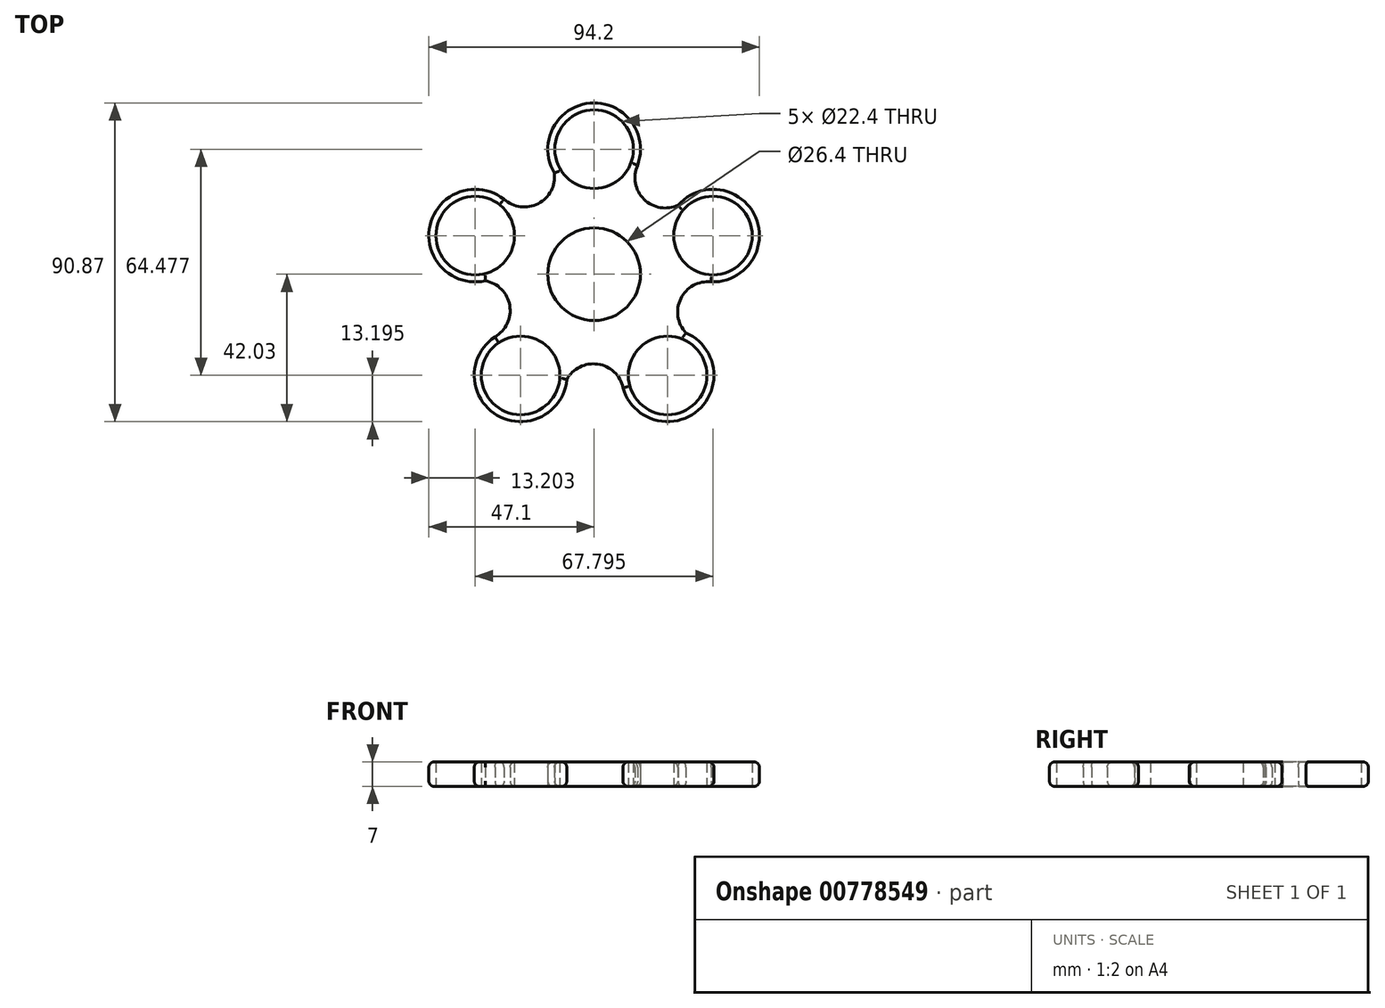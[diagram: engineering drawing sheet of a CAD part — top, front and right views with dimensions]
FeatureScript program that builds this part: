
annotation { "Feature Type Name" : "Feature", "Feature Type Description" : "" }
export const myFeature = defineFeature(function(context is Context, id is Id, definition is map)
    precondition{}
    {
        {
            var Q0;
            Q0=qCreatedBy(makeId("Top.planeOp"),FACE);
            var sketch = newSketch(context, id + "F0", { "sketchPlane" : qUnion([Q0])});
            skCircle(sketch, "E0", {"center": v(0, 0) * mm, "radius": 11.2 * mm});
            skCircle(sketch, "E1", {"center": v(0, 0) * mm, "radius": 13.2 * mm});
            skCircle(sketch, "E2", {"center": v(0, 35.64) * mm, "radius": 11.2 * mm});
            skCircle(sketch, "E3", {"center": v(0, 35.64) * mm, "radius": 13.2 * mm});
            skCircle(sketch, "E4.1.0", {"center": v(-33.9, 11.01) * mm, "radius": 11.2 * mm});
            skCircle(sketch, "E4.1.1", {"center": v(-33.9, 11.01) * mm, "radius": 13.2 * mm});
            skCircle(sketch, "E4.2.0", {"center": v(-20.95, -28.83) * mm, "radius": 11.2 * mm});
            skCircle(sketch, "E4.2.1", {"center": v(-20.95, -28.83) * mm, "radius": 13.2 * mm});
            skCircle(sketch, "E4.3.0", {"center": v(20.95, -28.83) * mm, "radius": 11.2 * mm});
            skCircle(sketch, "E4.3.1", {"center": v(20.95, -28.83) * mm, "radius": 13.2 * mm});
            skCircle(sketch, "E4.4.0", {"center": v(33.9, 11.01) * mm, "radius": 11.2 * mm});
            skCircle(sketch, "E4.4.1", {"center": v(33.9, 11.01) * mm, "radius": 13.2 * mm});
            skArc(sketch, "E5", {"start": v(12.37, 31.05) * mm, "mid": v(14.23, 21.35) * mm, "end": v(23.97, 19.71) * mm});
            skArc(sketch, "E6.1.0", {"start": v(-25.7, 21.36) * mm, "mid": v(-15.9, 20.13) * mm, "end": v(-11.34, 28.89) * mm});
            skArc(sketch, "E6.2.0", {"start": v(-28.26, -17.84) * mm, "mid": v(-24.06, -8.9) * mm, "end": v(-30.98, -1.86) * mm});
            skArc(sketch, "E6.3.0", {"start": v(8.24, -32.4) * mm, "mid": v(1.04, -25.64) * mm, "end": v(-7.8, -30.04) * mm});
            skArc(sketch, "E6.4.0", {"start": v(33.35, -2.17) * mm, "mid": v(24.7, -6.94) * mm, "end": v(26.15, -16.7) * mm});
            skSolve(sketch);
        }
        {
            var Q0;
            Q0=makeQuery(id+"F0.imprint","IMPRINT",FACE,{"disambiguationData":[TD([[makeQuery(id+"F0.imprint","IMPRINT",EDGE,{"derivedFrom":sQuery(id+"F0.wireOp",EDGE,"E1")}),-1.0]])]});
            var Q1;
            Q1=makeQuery(id+"F0.imprint","IMPRINT",FACE,{"disambiguationData":[TD([[makeQuery(id+"F0.imprint","IMPRINT",EDGE,{"derivedFrom":sQuery(id+"F0.wireOp",EDGE,"E4.2.0")}),-1.0]])]});
            var Q2;
            Q2=makeQuery(id+"F0.imprint","IMPRINT",FACE,{"disambiguationData":[TD([[makeQuery(id+"F0.imprint","IMPRINT",EDGE,{"derivedFrom":sQuery(id+"F0.wireOp",EDGE,"E4.3.0")}),-1.0]])]});
            var Q3;
            Q3=makeQuery(id+"F0.imprint","IMPRINT",FACE,{"disambiguationData":[TD([[makeQuery(id+"F0.imprint","IMPRINT",EDGE,{"derivedFrom":sQuery(id+"F0.wireOp",EDGE,"E4.4.0")}),-1.0]])]});
            var Q4;
            Q4=makeQuery(id+"F0.imprint","IMPRINT",FACE,{"disambiguationData":[TD([[makeQuery(id+"F0.imprint","IMPRINT",EDGE,{"derivedFrom":sQuery(id+"F0.wireOp",EDGE,"E2")}),-1.0]])]});
            var Q5;
            Q5=makeQuery(id+"F0.imprint","IMPRINT",FACE,{"disambiguationData":[TD([[makeQuery(id+"F0.imprint","IMPRINT",EDGE,{"derivedFrom":sQuery(id+"F0.wireOp",EDGE,"E4.1.0")}),-1.0]])]});
            extrude(context, id + "F1", {"entities" : qUnion([Q0, Q1, Q2, Q3, Q4, Q5]), "depth" : 7 * mm, "offsetDistance" : 25 * mm});
        }
        {
            var Q0;
            Q0=makeQuery(id+"F1.opExtrude","CAP_EDGE",EDGE,{"disambiguationData":[OSD([sQuery(id+"F0.wireOp",EDGE,"E5")])],"isStart":true});
            var Q1;
            Q1=makeQuery(id+"F1.opExtrude","CAP_EDGE",EDGE,{"disambiguationData":[OSD([sQuery(id+"F0.wireOp",EDGE,"E4.4.1")])],"isStart":true});
            var Q2;
            Q2=makeQuery(id+"F1.opExtrude","CAP_EDGE",EDGE,{"disambiguationData":[OSD([sQuery(id+"F0.wireOp",EDGE,"E6.4.0")])],"isStart":true});
            var Q3;
            Q3=makeQuery(id+"F1.opExtrude","CAP_EDGE",EDGE,{"disambiguationData":[OSD([sQuery(id+"F0.wireOp",EDGE,"E4.3.1")])],"isStart":true});
            var Q4;
            Q4=makeQuery(id+"F1.opExtrude","CAP_EDGE",EDGE,{"disambiguationData":[OSD([sQuery(id+"F0.wireOp",EDGE,"E6.3.0")])],"isStart":true});
            var Q5;
            Q5=makeQuery(id+"F1.opExtrude","CAP_EDGE",EDGE,{"disambiguationData":[OSD([sQuery(id+"F0.wireOp",EDGE,"E4.2.1")])],"isStart":true});
            var Q6;
            Q6=makeQuery(id+"F1.opExtrude","CAP_EDGE",EDGE,{"disambiguationData":[OSD([sQuery(id+"F0.wireOp",EDGE,"E6.2.0")])],"isStart":true});
            var Q7;
            Q7=makeQuery(id+"F1.opExtrude","CAP_EDGE",EDGE,{"disambiguationData":[OSD([sQuery(id+"F0.wireOp",EDGE,"E4.1.1")])],"isStart":true});
            var Q8;
            Q8=makeQuery(id+"F1.opExtrude","CAP_EDGE",EDGE,{"disambiguationData":[OSD([sQuery(id+"F0.wireOp",EDGE,"E3")])],"isStart":true});
            var Q9;
            Q9=makeQuery(id+"F1.opExtrude","CAP_EDGE",EDGE,{"disambiguationData":[OSD([sQuery(id+"F0.wireOp",EDGE,"E6.1.0")])],"isStart":true});
            var Q10;
            Q10=makeQuery(id+"F1.opExtrude","CAP_EDGE",EDGE,{"disambiguationData":[OSD([sQuery(id+"F0.wireOp",EDGE,"E5")])],"isStart":false});
            var Q11;
            Q11=makeQuery(id+"F1.opExtrude","CAP_EDGE",EDGE,{"disambiguationData":[OSD([sQuery(id+"F0.wireOp",EDGE,"E4.1.1")])],"isStart":false});
            var Q12;
            Q12=makeQuery(id+"F1.opExtrude","CAP_EDGE",EDGE,{"disambiguationData":[OSD([sQuery(id+"F0.wireOp",EDGE,"E6.1.0")])],"isStart":false});
            var Q13;
            Q13=makeQuery(id+"F1.opExtrude","CAP_EDGE",EDGE,{"disambiguationData":[OSD([sQuery(id+"F0.wireOp",EDGE,"E3")])],"isStart":false});
            var Q14;
            Q14=makeQuery(id+"F1.opExtrude","CAP_EDGE",EDGE,{"disambiguationData":[OSD([sQuery(id+"F0.wireOp",EDGE,"E4.4.1")])],"isStart":false});
            var Q15;
            Q15=makeQuery(id+"F1.opExtrude","CAP_EDGE",EDGE,{"disambiguationData":[OSD([sQuery(id+"F0.wireOp",EDGE,"E6.4.0")])],"isStart":false});
            var Q16;
            Q16=makeQuery(id+"F1.opExtrude","CAP_EDGE",EDGE,{"disambiguationData":[OSD([sQuery(id+"F0.wireOp",EDGE,"E4.3.1")])],"isStart":false});
            var Q17;
            Q17=makeQuery(id+"F1.opExtrude","CAP_EDGE",EDGE,{"disambiguationData":[OSD([sQuery(id+"F0.wireOp",EDGE,"E6.3.0")])],"isStart":false});
            var Q18;
            Q18=makeQuery(id+"F1.opExtrude","CAP_EDGE",EDGE,{"disambiguationData":[OSD([sQuery(id+"F0.wireOp",EDGE,"E4.2.1")])],"isStart":false});
            var Q19;
            Q19=makeQuery(id+"F1.opExtrude","CAP_EDGE",EDGE,{"disambiguationData":[OSD([sQuery(id+"F0.wireOp",EDGE,"E6.2.0")])],"isStart":false});
            fillet(context, id + "F2", {"entities" : qUnion([Q0, Q1, Q2, Q3, Q4, Q5, Q6, Q7, Q8, Q9, Q10, Q11, Q12, Q13, Q14, Q15, Q16, Q17, Q18, Q19]), "radius" : 1.5 * mm, "tangentPropagation" : true, "allowEdgeOverflow" : false});
        }
    });
